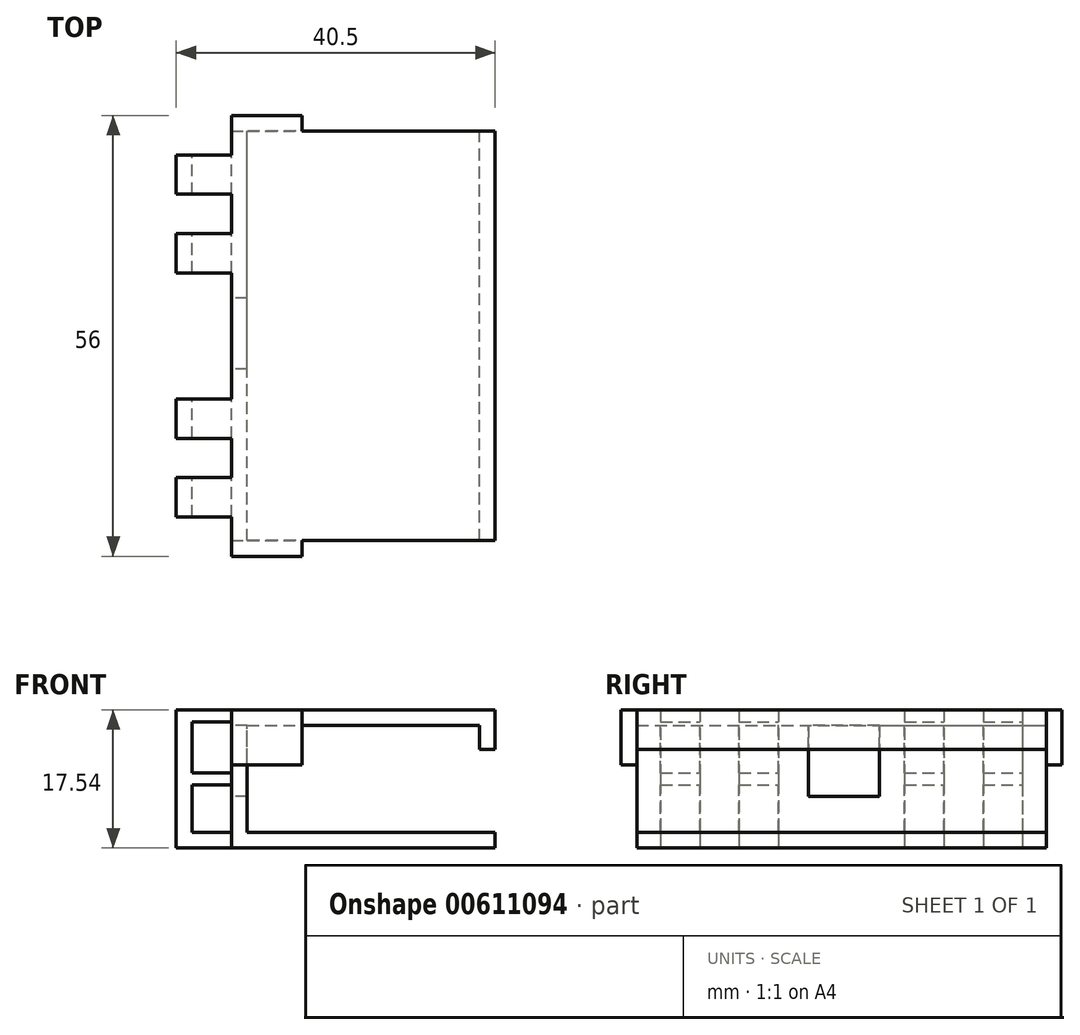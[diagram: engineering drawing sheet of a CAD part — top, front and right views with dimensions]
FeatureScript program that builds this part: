
annotation { "Feature Type Name" : "Feature", "Feature Type Description" : "" }
export const myFeature = defineFeature(function(context is Context, id is Id, definition is map)
    precondition{}
    {
        {
            var Q0;
            Q0=qCreatedBy(makeId("Front.planeOp"),FACE);
            var sketch = newSketch(context, id + "F0", { "sketchPlane" : qUnion([Q0])});
            skLineSegment(sketch, "E0", {"start": v(0, 0) * mm, "end": v(0, 13.54) * mm});
            skLineSegment(sketch, "E1", {"start": v(0, 13.54) * mm, "end": v(29.5, 13.54) * mm});
            skLineSegment(sketch, "E2", {"start": v(29.5, 13.54) * mm, "end": v(29.5, 10.54) * mm});
            skLineSegment(sketch, "E3", {"start": v(29.5, 10.54) * mm, "end": v(31.5, 10.54) * mm});
            skLineSegment(sketch, "E4", {"start": v(31.5, 10.54) * mm, "end": v(31.5, 15.54) * mm});
            skLineSegment(sketch, "E5", {"start": v(31.5, 15.54) * mm, "end": v(-2, 15.54) * mm});
            skLineSegment(sketch, "E6", {"start": v(-2, 15.54) * mm, "end": v(-2, -2) * mm});
            skLineSegment(sketch, "E7", {"start": v(-2, -2) * mm, "end": v(31.5, -2) * mm});
            skLineSegment(sketch, "E8", {"start": v(31.5, -2) * mm, "end": v(31.5, 0) * mm});
            skLineSegment(sketch, "E9", {"start": v(31.5, 0) * mm, "end": v(0, 0) * mm});
            skSolve(sketch);
        }
        {
            var Q0;
            Q0 = qSketchRegion(id + "F0", true);
            extrude(context, id + "F1", {"entities" : qUnion([Q0]), "depth" : 52 * mm, "offsetDistance" : 25 * mm});
        }
        {
            var Q0;
            Q0=makeQuery(id+"F1.opExtrude","SWEPT_FACE",FACE,{"disambiguationData":[OSD([sQuery(id+"F0.wireOp",EDGE,"E6")])]});
            var sketch = newSketch(context, id + "F2", { "sketchPlane" : qUnion([Q0])});
            skLineSegment(sketch, "E10.bottom", {"start": v(21.2, 13.54) * mm, "end": v(30.2, 13.54) * mm});
            skLineSegment(sketch, "E10.top", {"start": v(21.2, 4.54) * mm, "end": v(30.2, 4.54) * mm});
            skLineSegment(sketch, "E10.left", {"start": v(21.2, 13.54) * mm, "end": v(21.2, 4.54) * mm});
            skLineSegment(sketch, "E10.right", {"start": v(30.2, 13.54) * mm, "end": v(30.2, 4.54) * mm});
            skSolve(sketch);
        }
        {
            var Q0;
            Q0=makeQuery(id+"F2.imprint","IMPRINT",FACE,{"disambiguationData":[TD([[makeQuery(id+"F2.imprint","IMPRINT",EDGE,{"derivedFrom":sQuery(id+"F2.wireOp",EDGE,"E10.bottom")}),-1.0]])]});
            extrude(context, id + "F3", {"entities" : qUnion([Q0]), "operationType" : NewBodyOperationType.REMOVE, "endBound" : BoundingType.UP_TO_NEXT, "oppositeDirection" : true, "depth" : 25 * mm, "offsetDistance" : 25 * mm});
        }
        {
            var Q0;
            Q0=makeQuery(id+"F1.opExtrude","SWEPT_FACE",FACE,{"disambiguationData":[OSD([sQuery(id+"F0.wireOp",EDGE,"E6")])]});
            var sketch = newSketch(context, id + "F4", { "sketchPlane" : qUnion([Q0])});
            skLineSegment(sketch, "E11.bottom", {"start": v(18, 15.54) * mm, "end": v(13, 15.54) * mm});
            skLineSegment(sketch, "E11.top", {"start": v(18, -2) * mm, "end": v(13, -2) * mm});
            skLineSegment(sketch, "E11.left", {"start": v(18, 15.54) * mm, "end": v(18, -2) * mm});
            skLineSegment(sketch, "E11.right", {"start": v(13, 15.54) * mm, "end": v(13, -2) * mm});
            skLineSegment(sketch, "E12.bottom", {"start": v(3, 15.54) * mm, "end": v(8, 15.54) * mm});
            skLineSegment(sketch, "E12.top", {"start": v(3, -2) * mm, "end": v(8, -2) * mm});
            skLineSegment(sketch, "E12.left", {"start": v(3, 15.54) * mm, "end": v(3, -2) * mm});
            skLineSegment(sketch, "E12.right", {"start": v(8, 15.54) * mm, "end": v(8, -2) * mm});
            skLineSegment(sketch, "E13.bottom", {"start": v(34, 15.54) * mm, "end": v(39, 15.54) * mm});
            skLineSegment(sketch, "E13.top", {"start": v(34, -2) * mm, "end": v(39, -2) * mm});
            skLineSegment(sketch, "E13.left", {"start": v(34, 15.54) * mm, "end": v(34, -2) * mm});
            skLineSegment(sketch, "E13.right", {"start": v(39, 15.54) * mm, "end": v(39, -2) * mm});
            skLineSegment(sketch, "E14.bottom", {"start": v(44, 15.54) * mm, "end": v(49, 15.54) * mm});
            skLineSegment(sketch, "E14.top", {"start": v(44, -2) * mm, "end": v(49, -2) * mm});
            skLineSegment(sketch, "E14.left", {"start": v(44, 15.54) * mm, "end": v(44, -2) * mm});
            skLineSegment(sketch, "E14.right", {"start": v(49, 15.54) * mm, "end": v(49, -2) * mm});
            skSolve(sketch);
        }
        {
            var Q0;
            Q0=makeQuery(id+"F1.opExtrude","CAP_FACE",FACE,{"disambiguationData":[OSD([sQuery(id+"F0.wireOp",EDGE,"E0"),sQuery(id+"F0.wireOp",EDGE,"E1"),sQuery(id+"F0.wireOp",EDGE,"E2"),sQuery(id+"F0.wireOp",EDGE,"E3"),sQuery(id+"F0.wireOp",EDGE,"E4"),sQuery(id+"F0.wireOp",EDGE,"E5"),sQuery(id+"F0.wireOp",EDGE,"E6"),sQuery(id+"F0.wireOp",EDGE,"E7"),sQuery(id+"F0.wireOp",EDGE,"E8"),sQuery(id+"F0.wireOp",EDGE,"E9")])],"isStart":true});
            var sketch = newSketch(context, id + "F5", { "sketchPlane" : qUnion([Q0])});
            skLineSegment(sketch, "E15.bottom", {"start": v(2, 15.54) * mm, "end": v(-7, 15.54) * mm});
            skLineSegment(sketch, "E15.top", {"start": v(2, 8.54) * mm, "end": v(-7, 8.54) * mm});
            skLineSegment(sketch, "E15.left", {"start": v(2, 15.54) * mm, "end": v(2, 8.54) * mm});
            skLineSegment(sketch, "E15.right", {"start": v(-7, 15.54) * mm, "end": v(-7, 8.54) * mm});
            skSolve(sketch);
        }
        {
            var Q0;
            Q0 = qSketchRegion(id + "F5", true);
            extrude(context, id + "F6", {"entities" : qUnion([Q0]), "operationType" : NewBodyOperationType.ADD, "depth" : 2 * mm, "offsetDistance" : 25 * mm});
        }
        {
            var Q0;
            Q0=makeQuery(id+"F1.opExtrude","CAP_FACE",FACE,{"disambiguationData":[OSD([sQuery(id+"F0.wireOp",EDGE,"E0"),sQuery(id+"F0.wireOp",EDGE,"E1"),sQuery(id+"F0.wireOp",EDGE,"E2"),sQuery(id+"F0.wireOp",EDGE,"E3"),sQuery(id+"F0.wireOp",EDGE,"E4"),sQuery(id+"F0.wireOp",EDGE,"E5"),sQuery(id+"F0.wireOp",EDGE,"E6"),sQuery(id+"F0.wireOp",EDGE,"E7"),sQuery(id+"F0.wireOp",EDGE,"E8"),sQuery(id+"F0.wireOp",EDGE,"E9")])],"isStart":false});
            var sketch = newSketch(context, id + "F7", { "sketchPlane" : qUnion([Q0])});
            skLineSegment(sketch, "E16.bottom", {"start": v(-2, 15.54) * mm, "end": v(7, 15.54) * mm});
            skLineSegment(sketch, "E16.top", {"start": v(-2, 8.54) * mm, "end": v(7, 8.54) * mm});
            skLineSegment(sketch, "E16.left", {"start": v(-2, 15.54) * mm, "end": v(-2, 8.54) * mm});
            skLineSegment(sketch, "E16.right", {"start": v(7, 15.54) * mm, "end": v(7, 8.54) * mm});
            skSolve(sketch);
        }
        {
            var Q0;
            Q0 = qSketchRegion(id + "F7", true);
            extrude(context, id + "F8", {"entities" : qUnion([Q0]), "operationType" : NewBodyOperationType.ADD, "depth" : 2 * mm, "offsetDistance" : 25 * mm});
        }
        {
            var Q0;
            Q0 = qSketchRegion(id + "F4", true);
            extrude(context, id + "F9", {"entities" : qUnion([Q0]), "operationType" : NewBodyOperationType.ADD, "depth" : 7 * mm, "offsetDistance" : 25 * mm});
        }
        {
            var Q0;
            Q0=makeQuery(id+"F9.opExtrude","SWEPT_FACE",FACE,{"disambiguationData":[OSD([sQuery(id+"F4.wireOp",EDGE,"E12.left")])]});
            var sketch = newSketch(context, id + "F10", { "sketchPlane" : qUnion([Q0])});
            skLineSegment(sketch, "E17.bottom", {"start": v(2, 14.04) * mm, "end": v(7, 14.04) * mm});
            skLineSegment(sketch, "E17.top", {"start": v(2, 7.54) * mm, "end": v(7, 7.54) * mm});
            skLineSegment(sketch, "E17.left", {"start": v(2, 14.04) * mm, "end": v(2, 7.54) * mm});
            skLineSegment(sketch, "E17.right", {"start": v(7, 14.04) * mm, "end": v(7, 7.54) * mm});
            skLineSegment(sketch, "E18.bottom", {"start": v(2, 6.04) * mm, "end": v(7, 6.04) * mm});
            skLineSegment(sketch, "E18.top", {"start": v(2, 0) * mm, "end": v(7, 0) * mm});
            skLineSegment(sketch, "E18.left", {"start": v(2, 6.04) * mm, "end": v(2, 0) * mm});
            skLineSegment(sketch, "E18.right", {"start": v(7, 6.04) * mm, "end": v(7, 0) * mm});
            skSolve(sketch);
        }
        {
            var Q0;
            Q0=makeQuery(id+"F10.imprint","IMPRINT",FACE,{"disambiguationData":[TD([[makeQuery(id+"F10.imprint","IMPRINT",EDGE,{"derivedFrom":sQuery(id+"F10.wireOp",EDGE,"E17.bottom")}),-1.0]])]});
            var Q1;
            Q1=makeQuery(id+"F10.imprint","IMPRINT",FACE,{"disambiguationData":[TD([[makeQuery(id+"F10.imprint","IMPRINT",EDGE,{"derivedFrom":sQuery(id+"F10.wireOp",EDGE,"E18.bottom")}),-1.0]])]});
            extrude(context, id + "F11", {"entities" : qUnion([Q0, Q1]), "operationType" : NewBodyOperationType.REMOVE, "endBound" : BoundingType.THROUGH_ALL, "oppositeDirection" : true, "depth" : 25 * mm, "offsetDistance" : 25 * mm});
        }
    });
